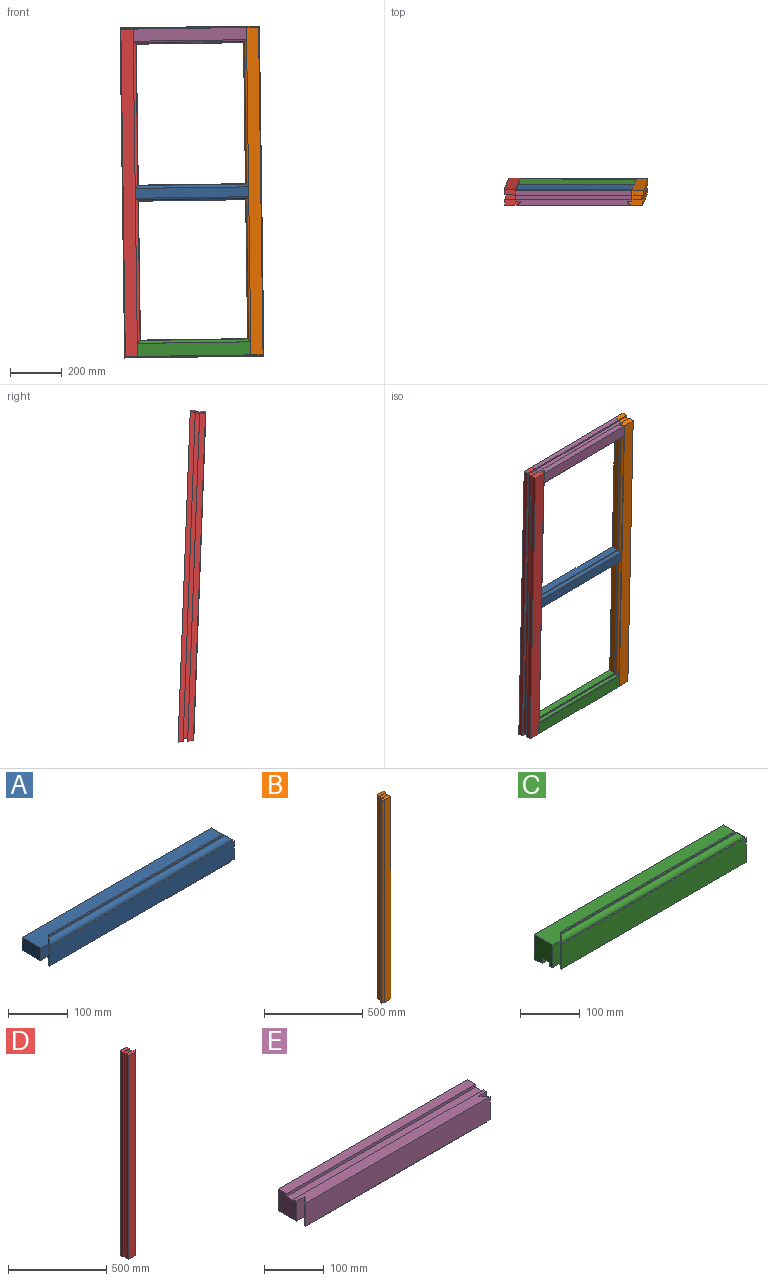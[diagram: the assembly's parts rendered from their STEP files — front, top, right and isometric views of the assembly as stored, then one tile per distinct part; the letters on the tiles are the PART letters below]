
ASSEMBLY  parts=5 mates=4
PART A: 26 faces, bbox 450x59x62 mm
  f0: plane 62x3mm, normal (-1,0,0), area 186mm2, adj f1,f2,f6,f16,f17,f18,f24,f25
  f1: plane 56x3mm, normal (0,1,0), area 168mm2, adj f0,f4,f15,f20
  f2: plane 26x18mm, normal (0,-1,0), area 468mm2, adj f0,f3,f21,f23
  f3: plane 44x26mm, normal (-1,0,0), area 1144mm2, adj f2,f21,f22,f23
  f4: cylinder r=9mm len=56mm, axis (0,0,-1), area 699.2mm2, adj f1,f5,f15,f20
  f5: plane 38x3mm, normal (-1,0,0), area 114mm2, adj f4,f13,f14,f19
  f6: plane 414x3mm, normal (0,-1,0), area 1242mm2, adj f0,f7,f20,f24
  f7: plane 62x3mm, normal (1,0,0), area 186mm2, adj f6,f8,f9,f16,f17,f18,f24,f25
  f8: plane 56x3mm, normal (0,1,0), area 168mm2, adj f7,f11,f15,f20
  f9: plane 26x18mm, normal (0,-1,0), area 468mm2, adj f7,f10,f21,f23
  f10: plane 44x26mm, normal (1,0,0), area 1144mm2, adj f9,f21,f22,f23
  f11: cylinder r=9mm len=56mm, axis (0,0,-1), area 699.2mm2, adj f8,f12,f15,f20
  f12: plane 38x3mm, normal (1,0,0), area 114mm2, adj f11,f13,f14,f19
  f13: plane 438x38mm, normal (0,-1,0), area 16644mm2, adj f5,f12,f14,f19
  f14: plane 438x3mm, normal (0,0,-1), area 1314mm2, adj f5,f12,f13,f15
  f15: cylinder r=9mm len=438mm, axis (1,0,0), area 6030.1mm2, adj f1,f4,f8,f11,f14,f16
  f16: plane 414x3mm, normal (0,-1,0), area 1242mm2, adj f0,f7,f15,f17
  f17: plane 414x3mm, normal (0,0,-1), area 1242mm2, adj f0,f7,f16,f18
  f18: plane 414x18mm, normal (0,1,0), area 7452mm2, adj f0,f7,f17,f21
  f19: plane 438x3mm, normal (0,0,1), area 1314mm2, adj f5,f12,f13,f20
  f20: cylinder r=9mm len=438mm, axis (1,0,0), area 6030.1mm2, adj f1,f4,f6,f8,f11,f19
  f21: plane 450x44mm, normal (0,0,-1), area 19800mm2, adj f2,f3,f9,f10,f18,f22
  f22: plane 450x26mm, normal (0,1,0), area 11700mm2, adj f3,f10,f21,f23
  f23: plane 450x44mm, normal (0,0,1), area 19800mm2, adj f2,f3,f9,f10,f22,f25
  f24: plane 414x3mm, normal (0,0,1), area 1242mm2, adj f0,f6,f7,f25
  f25: plane 414x18mm, normal (0,1,0), area 7452mm2, adj f0,f7,f23,f24
PART B: 19 faces, bbox 62x59x1276 mm
  f0: plane 44x19.35mm, normal (0,0,1), area 851.4mm2, adj f10,f11,f12,f14
  f1: plane 1265.51x47mm, normal (0,-1,0), area 59478.9mm2, adj f2,f9,f15,f18
  f2: plane 1265.89x3mm, normal (-1,0,0), area 3797.1mm2, adj f1,f3,f15,f18
  f3: cylinder r=9mm len=1267.03mm, axis (0,0,-1), area 17902mm2, adj f2,f4,f15,f18
  f4: plane 1267.03x3mm, normal (0,-1,0), area 3801.1mm2, adj f3,f5,f15,f18
  f5: plane 1267.41x3mm, normal (-1,0,0), area 3801.7mm2, adj f4,f6,f15,f18
  f6: plane 1267.41x18mm, normal (0,1,0), area 22813.4mm2, adj f5,f10,f15,f18
  f7: plane 1256.94x17.3mm, normal (1,0,0), area 21745.1mm2, adj f13,f14,f16,f17
  f8: plane 44x19.35mm, normal (0,-0.13,-0.99), area 858.2mm2, adj f10,f11,f12,f14
  f9: plane 1268.35x22.35mm, normal (1,0,0), area 28315.8mm2, adj f1,f13,f15,f18
  f10: plane 1276x44mm, normal (-1,0,0), area 55730.9mm2, adj f0,f6,f8,f11,f13,f14,f15,f16
  f11: plane 1276x44mm, normal (0,1,0), area 56144mm2, adj f0,f8,f10,f12
  f12: plane 1276x19.35mm, normal (1,0,0), area 24666.8mm2, adj f0,f8,f11,f14
  f13: plane 1268.35x41mm, normal (0,1,0), area 4238.3mm2, adj f7,f9,f10,f15,f16,f17,f18
  f14: plane 1273.54x44mm, normal (0,-1,0), area 8272mm2, adj f0,f7,f8,f10,f12,f16,f17
  f15: plane 59x22.35mm, normal (0,-0.13,-0.99), area 1114.8mm2, adj f1,f2,f3,f4,f5,f6,f9,f10
  f16: plane 38x17.3mm, normal (0,0,-1), area 657.4mm2, adj f7,f10,f13,f14
  f17: plane 38x17.3mm, normal (0,0,1), area 657.4mm2, adj f7,f10,f13,f14
  f18: plane 59x22.35mm, normal (0,0,1), area 1106mm2, adj f1,f2,f3,f4,f5,f6,f9,f10
PART C: 25 faces, bbox 450x59x70 mm
  f0: plane 52x44mm, normal (-1,0,0), area 2000.7mm2, adj f1,f11,f12,f14,f15,f22,f23,f24
  f1: plane 46.41x18mm, normal (0,-1,0), area 835.4mm2, adj f0,f2,f11,f15
  f2: plane 64.41x3mm, normal (-1,0,0), area 192.7mm2, adj f1,f3,f11,f16,f17,f18
  f3: plane 61.03x3mm, normal (0,1,0), area 183.1mm2, adj f2,f4,f11,f19
  f4: cylinder r=9mm len=61.03mm, axis (0,0,-1), area 806.3mm2, adj f3,f5,f11,f19
  f5: plane 50.89x3mm, normal (-1,0,0), area 152.1mm2, adj f4,f11,f20,f21
  f6: plane 46.41x18mm, normal (0,-1,0), area 835.4mm2, adj f7,f11,f13,f15
  f7: plane 64.41x3mm, normal (1,0,0), area 192.7mm2, adj f6,f8,f11,f16,f17,f18
  f8: plane 61.03x3mm, normal (0,1,0), area 183.1mm2, adj f7,f9,f11,f19
  f9: cylinder r=9mm len=61.03mm, axis (0,0,-1), area 806.3mm2, adj f8,f10,f11,f19
  f10: plane 50.89x3mm, normal (1,0,0), area 152.1mm2, adj f9,f11,f20,f21
  f11: plane 450x22.35mm, normal (0,-0.13,-0.99), area 9756mm2, adj f0,f1,f2,f3,f4,f5,f6,f7
  f12: plane 450x8.4mm, normal (0,1,0), area 3780.7mm2, adj f0,f11,f13,f22
  f13: plane 52x44mm, normal (1,0,0), area 2000.7mm2, adj f6,f11,f12,f14,f15,f22,f23,f24
  f14: plane 450x19.35mm, normal (0,-0.13,-0.99), area 8777.4mm2, adj f0,f13,f23,f24
  f15: plane 450x44mm, normal (0,0,1), area 19800mm2, adj f0,f1,f6,f13,f16,f24
  f16: plane 414x18mm, normal (0,1,0), area 7452mm2, adj f2,f7,f15,f17
  f17: plane 414x3mm, normal (0,0,1), area 1242mm2, adj f2,f7,f16,f18
  f18: plane 414x3mm, normal (0,-1,0), area 1242mm2, adj f2,f7,f17,f19
  f19: cylinder r=9mm len=438mm, axis (1,0,0), area 6030.1mm2, adj f3,f4,f8,f9,f18,f20
  f20: plane 438x3mm, normal (0,0,1), area 1314mm2, adj f5,f10,f19,f21
  f21: plane 438x50.51mm, normal (0,-1,0), area 22122.5mm2, adj f5,f10,f11,f20
  f22: plane 450x17.3mm, normal (0,0,-1), area 7785mm2, adj f0,f12,f13,f23
  f23: plane 450x10.6mm, normal (0,-1,0), area 4769.3mm2, adj f0,f13,f14,f22
  f24: plane 450x52mm, normal (0,1,0), area 23400mm2, adj f0,f13,f14,f15
PART D: 19 faces, bbox 62x59x1276 mm
  f0: plane 44x19.35mm, normal (0,0,1), area 851.4mm2, adj f10,f11,f12,f14
  f1: plane 1265.51x47mm, normal (0,-1,0), area 59478.9mm2, adj f2,f9,f15,f18
  f2: plane 1265.89x3mm, normal (1,0,0), area 3797.1mm2, adj f1,f3,f15,f18
  f3: cylinder r=9mm len=1267.03mm, axis (0,0,-1), area 17902mm2, adj f2,f4,f15,f18
  f4: plane 1267.03x3mm, normal (0,-1,0), area 3801.1mm2, adj f3,f5,f15,f18
  f5: plane 1267.41x3mm, normal (1,0,0), area 3801.7mm2, adj f4,f6,f15,f18
  f6: plane 1267.41x18mm, normal (0,1,0), area 22813.4mm2, adj f5,f10,f15,f18
  f7: plane 1256.94x17.3mm, normal (-1,0,0), area 21745.1mm2, adj f13,f14,f16,f17
  f8: plane 44x19.35mm, normal (0,-0.13,-0.99), area 858.2mm2, adj f10,f11,f12,f14
  f9: plane 1268.35x22.35mm, normal (-1,0,0), area 28315.8mm2, adj f1,f13,f15,f18
  f10: plane 1276x44mm, normal (1,0,0), area 55730.9mm2, adj f0,f6,f8,f11,f13,f14,f15,f16
  f11: plane 1276x44mm, normal (0,1,0), area 56144mm2, adj f0,f8,f10,f12
  f12: plane 1276x19.35mm, normal (-1,0,0), area 24666.8mm2, adj f0,f8,f11,f14
  f13: plane 1268.35x41mm, normal (0,1,0), area 4238.3mm2, adj f7,f9,f10,f15,f16,f17,f18
  f14: plane 1273.54x44mm, normal (0,-1,0), area 8272mm2, adj f0,f7,f8,f10,f12,f16,f17
  f15: plane 59x22.35mm, normal (0,-0.13,-0.99), area 1114.8mm2, adj f1,f2,f3,f4,f5,f6,f9,f10
  f16: plane 38x17.3mm, normal (0,0,-1), area 657.4mm2, adj f7,f10,f13,f14
  f17: plane 38x17.3mm, normal (0,0,1), area 657.4mm2, adj f7,f10,f13,f14
  f18: plane 59x22.35mm, normal (0,0,1), area 1106mm2, adj f1,f2,f3,f4,f5,f6,f9,f10
PART E: 25 faces, bbox 450x59x62 mm
  f0: plane 44x44mm, normal (-1,0,0), area 1810.2mm2, adj f1,f6,f13,f19,f21,f22,f23,f24
  f1: plane 41x18mm, normal (0,-1,0), area 738mm2, adj f0,f2,f13,f22
  f2: plane 59x3mm, normal (-1,0,0), area 177mm2, adj f1,f3,f13,f17,f18,f20
  f3: plane 56x3mm, normal (0,1,0), area 168mm2, adj f2,f4,f13,f16
  f4: cylinder r=9mm len=56mm, axis (0,0,-1), area 745.4mm2, adj f3,f5,f13,f16
  f5: plane 47x3mm, normal (-1,0,0), area 141mm2, adj f4,f13,f14,f15
  f6: plane 450x19.35mm, normal (0,0,1), area 8707.5mm2, adj f0,f7,f23,f24
  f7: plane 44x44mm, normal (1,0,0), area 1810.2mm2, adj f6,f8,f13,f19,f21,f22,f23,f24
  f8: plane 41x18mm, normal (0,-1,0), area 738mm2, adj f7,f9,f13,f22
  f9: plane 59x3mm, normal (1,0,0), area 177mm2, adj f8,f10,f13,f17,f18,f20
  f10: plane 56x3mm, normal (0,1,0), area 168mm2, adj f9,f11,f13,f16
  f11: cylinder r=9mm len=56mm, axis (0,0,-1), area 745.4mm2, adj f10,f12,f13,f16
  f12: plane 47x3mm, normal (1,0,0), area 141mm2, adj f11,f13,f14,f15
  f13: plane 450x22.35mm, normal (0,0,1), area 9678.3mm2, adj f0,f1,f2,f3,f4,f5,f7,f8
  f14: plane 438x47mm, normal (0,-1,0), area 20586mm2, adj f5,f12,f13,f15
  f15: plane 438x3mm, normal (0,0,-1), area 1314mm2, adj f5,f12,f14,f16
  f16: cylinder r=9mm len=438mm, axis (1,0,0), area 6030.1mm2, adj f3,f4,f10,f11,f15,f17
  f17: plane 414x3mm, normal (0,-1,0), area 1242mm2, adj f2,f9,f16,f18
  f18: plane 414x3mm, normal (0,0,-1), area 1242mm2, adj f2,f9,f17,f20
  f19: plane 450x3mm, normal (0,1,0), area 1350mm2, adj f0,f7,f13,f21
  f20: plane 414x18mm, normal (0,1,0), area 7452mm2, adj f2,f9,f18,f22
  f21: plane 450x17.3mm, normal (0,0,1), area 7785mm2, adj f0,f7,f19,f23
  f22: plane 450x44mm, normal (0,0,-1), area 19800mm2, adj f0,f1,f7,f8,f20,f24
  f23: plane 450x6mm, normal (0,-1,0), area 2700mm2, adj f0,f6,f7,f21
  f24: plane 450x44mm, normal (0,1,0), area 19800mm2, adj f0,f6,f7,f22
PLACE A rot(axis=(0.94,-0.35,-0.08),2.3deg) t=(-881.6,-50.09,-1334.7)mm
PLACE B rot(axis=(0.94,-0.35,-0.08),2.3deg) t=(-881.65,-50.24,-1330.7)mm
PLACE C rot(axis=(0.94,-0.35,-0.08),2.3deg) t=(-881.65,-50.24,-1330.7)mm
PLACE D rot(axis=(0.94,-0.35,-0.08),2.3deg) t=(-881.65,-50.24,-1330.7)mm
PLACE E rot(axis=(0.94,-0.35,-0.08),2.3deg) t=(-881.65,-50.24,-1330.7)mm
MATE fastened D.f10 <-> C.f0  axis (1,0,0.01) through (-217.35,-63.68,-1277.82)mm
MATE fastened E.f7 <-> B.f10  axis (1,0,0.01) through (215.11,-112.12,2.09)mm
MATE fastened A.f3 <-> D.f10  axis (-1,0,-0.01) through (-226.06,-77.49,-641.18)mm
MATE fastened E.f0 <-> D.f10  axis (-1,0,-0.01) through (-234.84,-110.67,-4.03)mm
